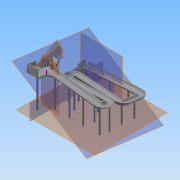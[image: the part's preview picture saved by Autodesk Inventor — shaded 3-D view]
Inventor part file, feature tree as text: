
AUTODESK INVENTOR PART (.ipt)
format: ipt  version: 2015 (Build 190159000, 159)  size: 1,478,144 bytes
history: native  units: mm
features: sketch x47, extrude x28, plane x15, sweep x5, projected_geometry x5, other x4, fillet x2, loft x1
ambient origin geometry x8: Origin, YZ Plane, XZ Plane, XY Plane, X Axis, Y Axis, Z Axis, Center Point
bodies: Body1 (feature_tree)
feature tree (107):
  other  "實體1"
  extrude  "擠出1"  Depth=12.0mm
  plane  "工作平面1"
  sketch  "草圖2"
  sketch  "草圖3"
  plane  "工作平面3"
  plane  "工作平面4"
  extrude  "擠出5"  Depth=14.0mm
  plane  "工作平面5"
  sketch  "草圖9"
  sketch  "草圖10"
  plane  "工作平面7"
  sweep  "掃掠2"
  plane  "工作平面8"
  extrude  "擠出7"  Depth=5.0mm TaperAngle=0.0deg
  extrude  "擠出8"  Depth=2.0mm
  plane  "工作平面10"
  sweep  "掃掠3"
  sketch  "草圖15"
  sweep  "掃掠4"
  sketch  "草圖18"
  sweep  "掃掠5"
  plane  "工作平面11"
  extrude  "擠出9"  TaperAngle=0.0deg  [1 undecoded]
  fillet  "圓角1"  [1 undecoded]
  sweep  "掃掠6"
  loft  "斷面混成1"
  fillet  "圓角2"  Radius=10.0mm
  plane  "工作平面12"
  extrude  "擠出10"  Depth=10.0mm
  extrude  "擠出11"  Depth=10.0mm
  sketch  "草圖25"
  plane  "工作平面13"
  extrude  "擠出12"  Depth=10.0mm
  extrude  "擠出13"  Depth=10.0mm
  extrude  "擠出14"  TaperAngle=0.0deg  [1 undecoded]
  extrude  "擠出15"  Depth=12.5mm TaperAngle=0.0deg
  other  "迴轉1"
  extrude  "擠出16"  Depth=20.0mm
  extrude  "擠出17"  TaperAngle=0.0deg  [1 undecoded]
  extrude  "擠出18"  TaperAngle=0.0deg  [1 undecoded]
  extrude  "擠出19"  TaperAngle=0.0deg  [1 undecoded]
  plane  "工作平面14"
  sketch  "草圖34"
  extrude  "擠出20"  Depth=2.0mm
  plane  "工作平面15"
  extrude  "擠出21"  Depth=3.0mm
  extrude  "擠出22"  Depth=3.0mm
  extrude  "擠出23"  Depth=3.0mm
  extrude  "擠出24"  Depth=3.0mm
  sketch  "草圖40"
  extrude  "擠出25"  Depth=3.0mm
  extrude  "擠出26"  Depth=3.0mm
  extrude  "擠出27"  Depth=3.0mm
  extrude  "擠出28"  Depth=3.0mm
  extrude  "擠出29"  Depth=3.0mm
  extrude  "擠出30"  Depth=3.0mm
  extrude  "擠出31"  Depth=3.0mm
  extrude  "擠出32"  Depth=3.0mm
  sketch  "3D 草圖1"
  sketch  "草圖1"
  other  "參考1"
  projected_geometry  "投影迴路1"
  plane  "工作平面2"
  sketch  "草圖8"
  other  "參考2"
  plane  "工作平面6"
  sketch  "草圖11"
  sketch  "草圖12"
  projected_geometry  "投影迴路3"
  sketch  "草圖13"
  plane  "工作平面9"
  sketch  "草圖14"
  sketch  "草圖16"
  sketch  "草圖17"
  sketch  "草圖19"
  sketch  "3D 草圖2"
  sketch  "草圖20"
  sketch  "草圖21"
  sketch  "3D 草圖3"
  sketch  "草圖22"
  sketch  "草圖23"
  sketch  "草圖24"
  sketch  "草圖26"
  sketch  "草圖27"
  sketch  "草圖28"
  sketch  "草圖29"
  sketch  "草圖30"
  sketch  "草圖31"
  sketch  "草圖32"
  sketch  "草圖33"
  sketch  "草圖35"
  sketch  "草圖36"
  sketch  "草圖37"
  sketch  "草圖38"
  sketch  "草圖39"
  projected_geometry  "投影迴路4"
  projected_geometry  "投影迴路5"
  sketch  "草圖42"
  projected_geometry  "投影迴路6"
  sketch  "草圖43"
  sketch  "草圖44"
  sketch  "草圖45"
  sketch  "草圖46"
  sketch  "草圖47"
  sketch  "草圖48"
  sketch  "草圖49"
note: 6 required parameter values undecoded (feature->parameter linkage not recoverable at this tier; creation-order binding heuristic only, values carry confidence <= 0.55)
